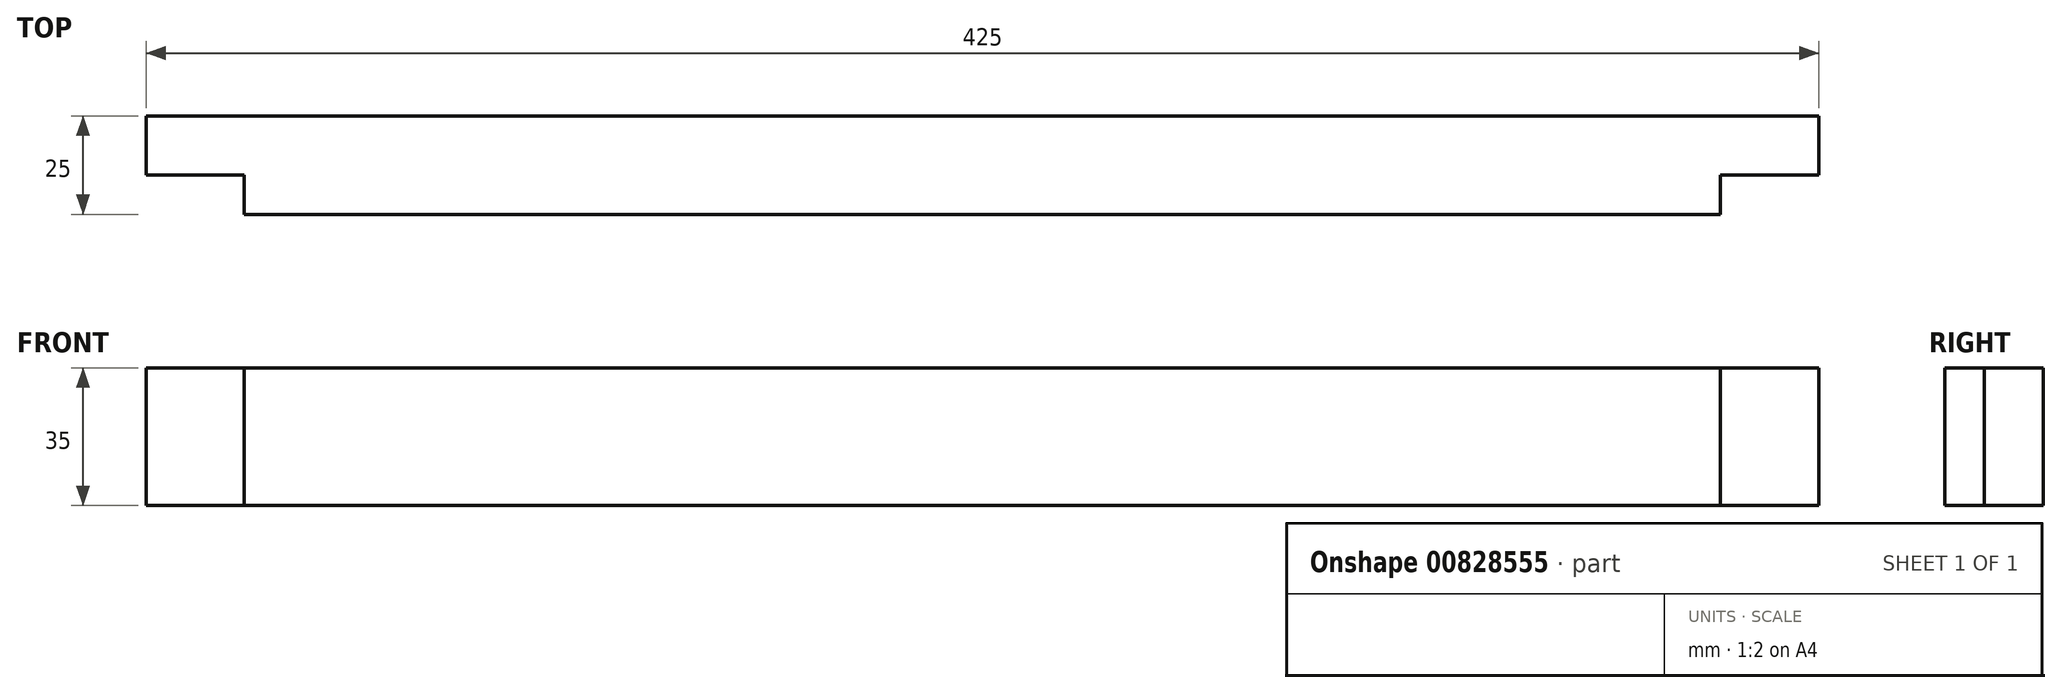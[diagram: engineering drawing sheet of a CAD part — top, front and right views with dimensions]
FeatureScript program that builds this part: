
annotation { "Feature Type Name" : "Feature", "Feature Type Description" : "" }
export const myFeature = defineFeature(function(context is Context, id is Id, definition is map)
    precondition{}
    {
        {
            var Q0;
            Q0=qCreatedBy(makeId("Front.planeOp"),FACE);
            var sketch = newSketch(context, id + "F0", { "sketchPlane" : qUnion([Q0])});
            skLineSegment(sketch, "E0.bottom", {"start": v(-212.5, 35) * mm, "end": v(212.5, 35) * mm});
            skLineSegment(sketch, "E0.top", {"start": v(-212.5, 0) * mm, "end": v(212.5, 0) * mm});
            skLineSegment(sketch, "E0.left", {"start": v(-212.5, 35) * mm, "end": v(-212.5, 0) * mm});
            skLineSegment(sketch, "E0.right", {"start": v(212.5, 35) * mm, "end": v(212.5, 0) * mm});
            skSolve(sketch);
        }
        {
            var Q0;
            Q0=qSketchRegion(id+"F0",true);
            extrude(context, id + "F1", {"entities" : qUnion([Q0]), "depth" : 15 * mm, "offsetDistance" : 25 * mm});
        }
        {
            var Q0;
            Q0=makeQuery(id+"F1.opExtrude","CAP_FACE",FACE,{"disambiguationData":[OSD([sQuery(id+"F0.wireOp",EDGE,"E0.bottom"),sQuery(id+"F0.wireOp",EDGE,"E0.top"),sQuery(id+"F0.wireOp",EDGE,"E0.left"),sQuery(id+"F0.wireOp",EDGE,"E0.right")])],"isStart":false});
            var sketch = newSketch(context, id + "F2", { "sketchPlane" : qUnion([Q0])});
            skLineSegment(sketch, "E1.bottom", {"start": v(-187.5, 35) * mm, "end": v(187.5, 35) * mm});
            skLineSegment(sketch, "E1.top", {"start": v(-187.5, 0) * mm, "end": v(187.5, 0) * mm});
            skLineSegment(sketch, "E1.left", {"start": v(-187.5, 35) * mm, "end": v(-187.5, 0) * mm});
            skLineSegment(sketch, "E1.right", {"start": v(187.5, 35) * mm, "end": v(187.5, 0) * mm});
            skSolve(sketch);
        }
        {
            var Q0;
            Q0=qSketchRegion(id+"F2",true);
            extrude(context, id + "F3", {"entities" : qUnion([Q0]), "operationType" : NewBodyOperationType.ADD, "depth" : 10 * mm, "offsetDistance" : 25 * mm});
        }
    });
